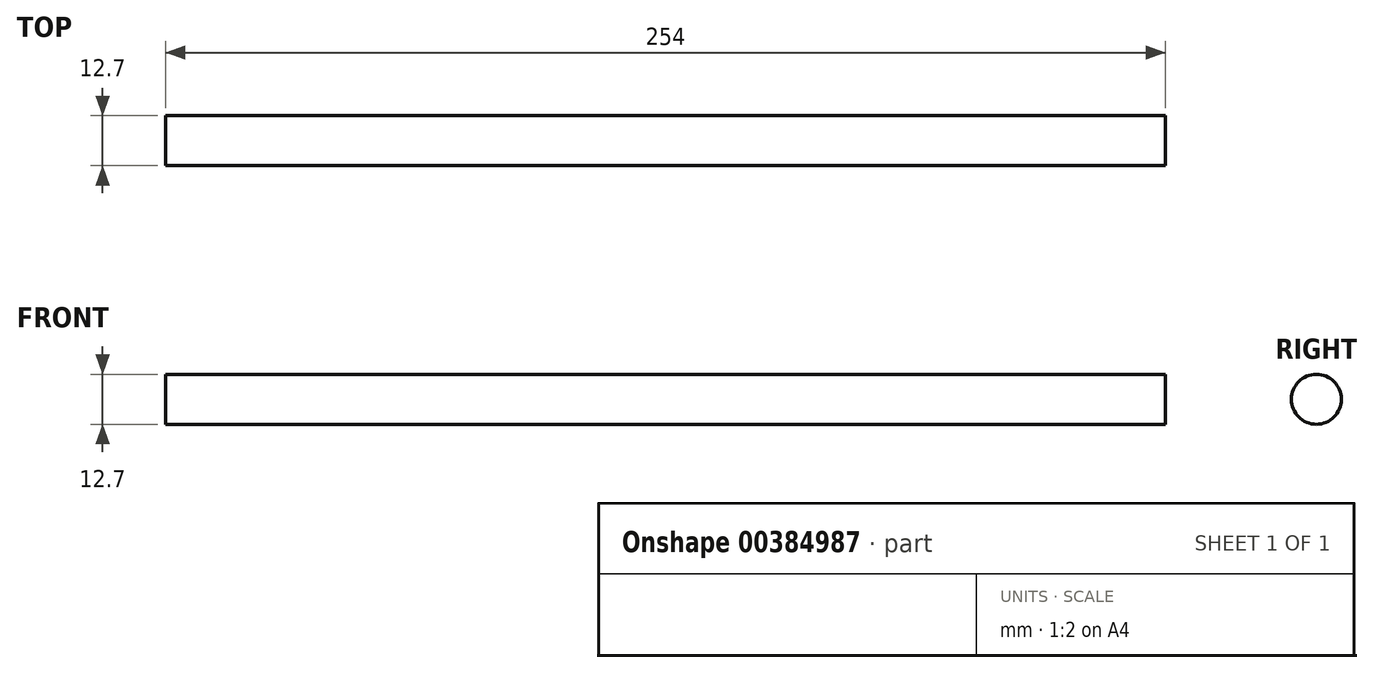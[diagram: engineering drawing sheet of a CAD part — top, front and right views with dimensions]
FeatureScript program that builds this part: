
annotation { "Feature Type Name" : "Feature", "Feature Type Description" : "" }
export const myFeature = defineFeature(function(context is Context, id is Id, definition is map)
    precondition{}
    {
        {
            var Q0;
            Q0=qCreatedBy(makeId("Right.planeOp"),FACE);
            var sketch = newSketch(context, id + "F0", { "sketchPlane" : qUnion([Q0])});
            skCircle(sketch, "E0", {"center": v(0, 0) * mm, "radius": 6.35 * mm});
            skCircle(sketch, "E1", {"center": v(0, 24.13) * mm, "radius": 33.02 * mm});
            skSolve(sketch);
        }
        {
            var Q0;
            Q0=makeQuery(id+"F0.imprint","IMPRINT",FACE,{"disambiguationData":[TD([[makeQuery(id+"F0.imprint","IMPRINT",EDGE,{"derivedFrom":sQuery(id+"F0.wireOp",EDGE,"E0")}),1.0]])]});
            extrude(context, id + "F1", {"entities" : qUnion([Q0]), "endBound" : BoundingType.SYMMETRIC, "depth" : 254 * mm, "offsetDistance" : 25.4 * mm});
        }
    });
